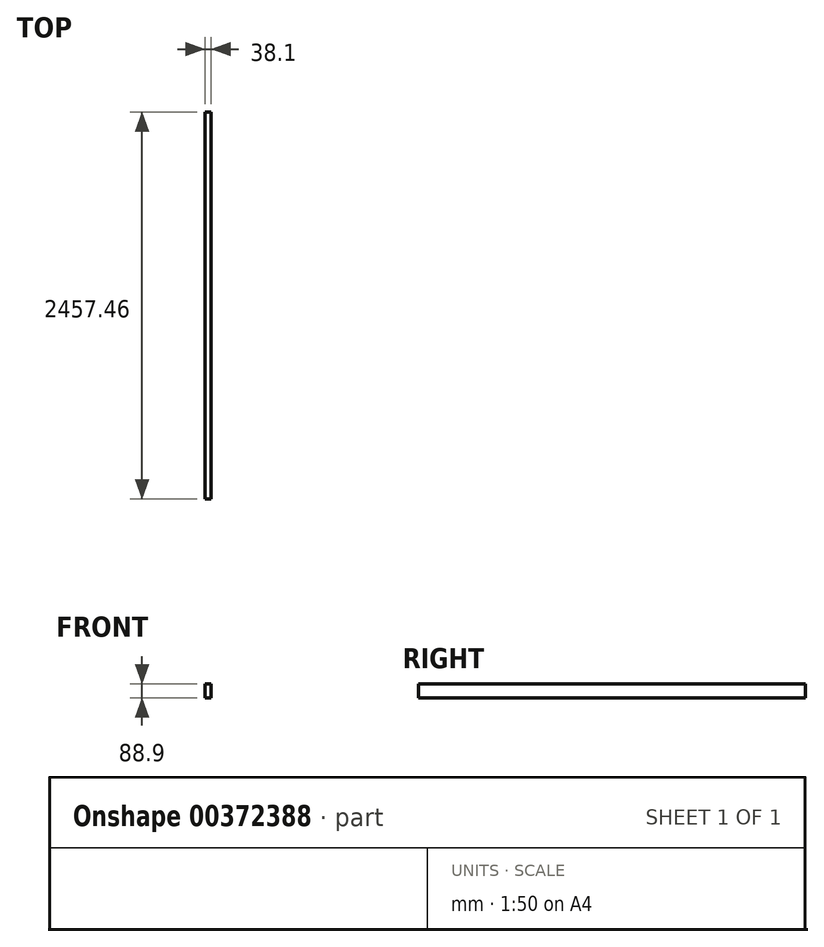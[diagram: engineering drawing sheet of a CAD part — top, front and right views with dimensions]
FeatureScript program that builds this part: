
annotation { "Feature Type Name" : "Feature", "Feature Type Description" : "" }
export const myFeature = defineFeature(function(context is Context, id is Id, definition is map)
    precondition{}
    {
        {
            var Q0;
            Q0=qCreatedBy(makeId("Front.planeOp"),FACE);
            var sketch = newSketch(context, id + "F0", { "sketchPlane" : qUnion([Q0])});
            skLineSegment(sketch, "E0.bottom", {"start": v(-19.05, 44.45) * mm, "end": v(19.05, 44.45) * mm});
            skLineSegment(sketch, "E0.top", {"start": v(-19.05, -44.45) * mm, "end": v(19.05, -44.45) * mm});
            skLineSegment(sketch, "E0.left", {"start": v(-19.05, 44.45) * mm, "end": v(-19.05, -44.45) * mm});
            skLineSegment(sketch, "E0.right", {"start": v(19.05, 44.45) * mm, "end": v(19.05, -44.45) * mm});
            skPoint(sketch, "E0.middle", {"position": v(0, 0) * mm});
            skSolve(sketch);
        }
        {
            var Q0;
            Q0=qSketchRegion(id+"F0",true);
            extrude(context, id + "F1", {"entities" : qUnion([Q0]), "endBound" : BoundingType.SYMMETRIC, "oppositeDirection" : true, "depth" : 2457.45 * mm});
        }
    });
